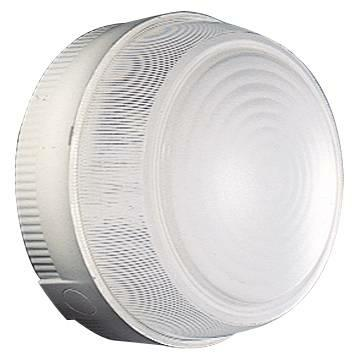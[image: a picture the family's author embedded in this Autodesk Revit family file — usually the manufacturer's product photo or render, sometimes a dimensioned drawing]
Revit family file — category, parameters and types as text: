
# Revit family: Lighting-CommercialSector-GEWISS-TONDAES-LUMINAIRES_180
name_source: partatom
category: Apparecchi per illuminazione
units: mm (PartAtom-declared; Revit-internal decimal feet)

## family parameters
Condiviso = No
Host = Superficie
Numero OmniClass = 23.80.70.00
Punto di calcolo locali = Sì
Quota connettore circolare = Usa diametro
Sorgente d'illuminazione = Sì
Taglio con vuoti quando caricato = No
Tipo di parte = Normale
Titolo OmniClass = Lighting

## types (1)
- GW80651 - For lamp E27 60W - Grey - IP44
    Angolo inclinazione = 0.00°
    Application = Indoor / Outdoor
    Carico apparente = 60 VA
    Catalogue = LIGHTING
    Catalogue Range = TONDA ES
    Colour = Grey RAL 7035
    Commenti sul wattaggio = 60W
    Descrizione = TONDA ES 180 60W E27 IP44 RAL7035
    EAN code = 8011564068773
    Efficiency class of compatible lamps = D ÷ A+
    Efficiency class of the lamp supplied = D ÷ A+
    Electrocod = 2415
    File diagramma fotometrico = GW80651-80651387.IES
    Filtro dei colori = 16777215
    Glow Wire Test = 850°C
    IDF = 894350d0-3539-4544-80d6-16fdae80d8dc
    IDT = 1579acc9-57b9-4df1-98d5-0dac6674b181
    IP degree = IP44
    Immagine tipo = GW80651.jpg
    Insulation class = II
    Lamp holder = E27
    Lamp power = 60W
    Lampada = E27
    Max lamp power = 60W
    Modello = GW80651
    Numero di poli = 2
    Produttore = GEWISS S.p.A.
    Prospetto di default = 1219 mm
    SEO = Luminaire
    Shock resistance = IK10
    Technical sheet = https://www.gewiss.com
    URL = https://www.gewiss.com
    Variazione temperatura colore lampada con luminosità attenuata = <Nessuno>
    Version file RFA = 20.11
    Voltaggio = 230 V
    Weight (kg) = 0,3
    Weight (kg): = 0,3
